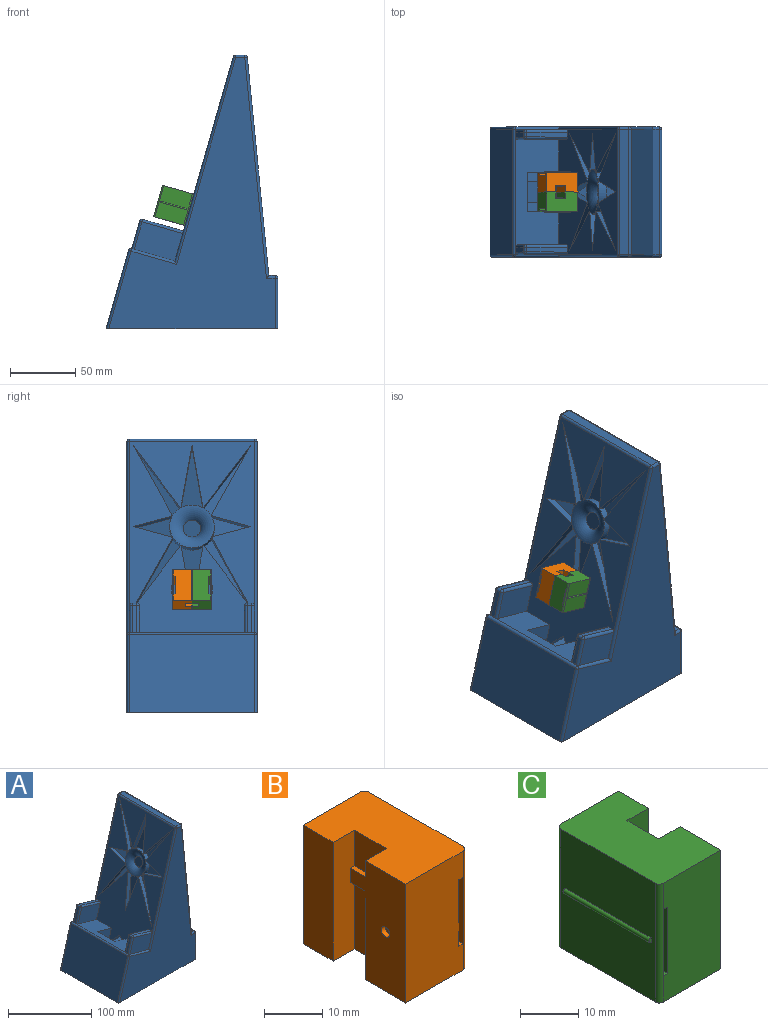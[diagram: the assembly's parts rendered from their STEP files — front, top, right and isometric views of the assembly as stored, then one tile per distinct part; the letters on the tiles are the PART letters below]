
ASSEMBLY  parts=3 mates=2
PART A: 139 faces, bbox 131.9x100x210.6 mm
  f0: plane 201.07x93mm, normal (0.96,0,-0.27), area 16114.9mm2, adj f1,f2,f3,f22,f23,f24,f25,f26
  f1: plane 6.2x1.71mm, normal (0.02,0,-1), area 5.3mm2, adj f0,f3,f137
  f2: plane 6.2x1.71mm, normal (0.02,0,-1), area 5.3mm2, adj f0,f98,f138
  f3: plane 24.74x13.23mm, normal (0,-1,0), area 152mm2, adj f0,f1,f11,f100
  f4: plane 5x1.82mm, normal (0.42,-0.91,0), area 5mm2, adj f9,f127,f134,f135,f136
  f5: plane 5x1.98mm, normal (0.99,-0.13,0), area 5mm2, adj f9,f125,f131,f132,f133
  f6: plane 5x1.98mm, normal (-0.99,0.13,0), area 5mm2, adj f9,f125,f131,f132,f133
  f7: plane 5x1.43mm, normal (-0.71,-0.7,0), area 5mm2, adj f9,f124,f128,f129,f130
  f8: plane 5x1.43mm, normal (0.71,0.7,0), area 5mm2, adj f9,f124,f128,f129,f130
  f9: plane 121.48x32.21mm, normal (0,0,1), area 3070.3mm2, adj f4,f5,f6,f7,f8,f16,f17,f24
  f10: plane 96x33.08mm, normal (0.27,0,0.96), area 2022.9mm2, adj f11,f20,f21,f57,f84,f88,f89,f104
  f11: plane 200.88x96mm, normal (-0.96,0,0.27), area 12526.6mm2, adj f3,f10,f20,f21,f24,f25,f27,f28
  f12: plane 131.88x100mm, normal (0,0,-1), area 13184.7mm2, adj f13,f51,f53,f85,f91,f92,f93,f97
  f13: plane 208x127.8mm, normal (0,-1,0), area 12025.5mm2, adj f12,f18,f73,f77,f82,f84,f85,f93
  f14: plane 96x5mm, normal (0,0,1), area 479.5mm2, adj f18,f19,f52,f95
  f15: plane 16x9.77mm, normal (0,0,-1), area 156.4mm2, adj f16,f17,f54,f92
  f16: plane 13.88x8.4mm, normal (0,1,0), area 80.6mm2, adj f9,f15,f23,f54,f65,f92
  f17: plane 13.88x8.4mm, normal (0,-1,0), area 80.6mm2, adj f9,f15,f22,f54,f61,f92
  f18: cylinder r=2mm len=6.81mm, axis (-1,0,0), area 17.8mm2, adj f13,f14,f73,f94
  f19: cylinder r=2mm len=6.81mm, axis (1,0,0), area 17.8mm2, adj f14,f51,f75,f96
  f20: plane 51.2x36.71mm, normal (0,-1,0), area 1128.6mm2, adj f10,f11,f57,f58,f70,f71,f72
  f21: plane 51.2x36.71mm, normal (0,1,0), area 1128.6mm2, adj f10,f11,f57,f58,f67,f68,f69
  f22: plane 77.33x40mm, normal (0,0,1), area 2508.9mm2, adj f0,f17,f25,f54,f56,f61,f62,f63
  f23: plane 77.33x37mm, normal (0,0,1), area 2312.4mm2, adj f0,f16,f24,f54,f55,f64,f65,f66
  f24: plane 37.7x8.4mm, normal (0,1,0), area 234.5mm2, adj f0,f9,f11,f23,f58,f59,f60,f64
  f25: plane 37.7x8.4mm, normal (0,-1,0), area 234.5mm2, adj f0,f9,f11,f22,f58,f59,f60,f62
  f26: cylinder r=17.15mm len=7.66mm, axis (-0.96,0,0.27), area 52.7mm2, adj f0,f27,f28,f101
  f27: plane 49.59x36.3mm, normal (-0.16,0.81,-0.57), area 365.4mm2, adj f0,f11,f26,f28,f101
  f28: plane 55.63x30.11mm, normal (0.13,-0.88,0.45), area 377.4mm2, adj f0,f11,f26,f27,f101
  f29: cylinder r=17.15mm len=17.03mm, axis (-0.96,0,0.27), area 105.4mm2, adj f0,f30,f31,f101
  f30: plane 49.43x19.37mm, normal (0.05,-0.99,0.16), area 298.6mm2, adj f0,f11,f29,f31,f101
  f31: plane 49.56x19.41mm, normal (0.05,0.99,0.16), area 299.6mm2, adj f0,f11,f29,f30,f101
  f32: cylinder r=17.15mm len=7.57mm, axis (-0.96,0,0.27), area 52.7mm2, adj f0,f33,f34,f101
  f33: plane 55.41x30.24mm, normal (-0.13,-0.88,-0.46), area 376.5mm2, adj f0,f11,f32,f34,f101
  f34: plane 49.46x36.53mm, normal (0.16,0.81,0.57), area 365.5mm2, adj f0,f11,f32,f33,f101
  f35: cylinder r=17.15mm len=17.98mm, axis (-0.96,0,0.27), area 105.2mm2, adj f0,f36,f37,f101
  f36: plane 30.05x9.7mm, normal (-0.26,-0.27,-0.93), area 184.7mm2, adj f0,f11,f35,f37,f101
  f37: plane 30.18x9.92mm, normal (0.26,-0.27,0.92), area 185.8mm2, adj f0,f11,f35,f36,f101
  f38: cylinder r=17.15mm len=17.03mm, axis (-0.96,0,0.27), area 105.4mm2, adj f0,f39,f40,f101
  f39: plane 49.44x19.36mm, normal (-0.05,0.99,-0.16), area 298.6mm2, adj f0,f11,f38,f40,f101
  f40: plane 49.56x19.4mm, normal (-0.05,-0.99,-0.16), area 299.6mm2, adj f0,f11,f38,f39,f101
  f41: cylinder r=17.15mm len=7.57mm, axis (-0.96,0,0.27), area 52.7mm2, adj f0,f42,f43,f101
  f42: plane 55.42x30.24mm, normal (0.13,0.88,0.46), area 376.5mm2, adj f0,f11,f41,f43,f101
  f43: plane 49.47x36.53mm, normal (-0.16,-0.81,-0.57), area 365.5mm2, adj f0,f11,f41,f42,f101
  f44: cylinder r=17.15mm len=7.66mm, axis (-0.96,0,0.27), area 52.7mm2, adj f0,f45,f46,f101
  f45: plane 49.59x36.3mm, normal (0.16,-0.81,0.57), area 365.4mm2, adj f0,f11,f44,f46,f101
  f46: plane 55.63x30.11mm, normal (-0.13,0.88,-0.45), area 377.4mm2, adj f0,f11,f44,f45,f101
  f47: cylinder r=17.15mm len=17.98mm, axis (-0.96,0,0.27), area 105.2mm2, adj f0,f48,f49,f101
  f48: plane 30.05x9.62mm, normal (0.27,0.27,0.93), area 184.5mm2, adj f0,f11,f47,f49,f101
  f49: plane 30.18x10mm, normal (-0.26,0.28,-0.92), area 185.9mm2, adj f0,f11,f47,f48,f101
  f50: plane 96x6.98mm, normal (0,0,1), area 669.7mm2, adj f76,f77,f80,f81
  f51: plane 208x127.8mm, normal (0,1,0), area 12025.5mm2, adj f12,f19,f75,f80,f86,f88,f91,f97
  f52: plane 167.24x96mm, normal (1,0,0.1), area 16132.7mm2, adj f14,f73,f75,f76
  f53: plane 96x60.08mm, normal (-0.96,0,0.27), area 5998.6mm2, adj f12,f85,f89,f91
  f54: plane 201.07x93mm, normal (-1,0,-0.1), area 18661.8mm2, adj f0,f15,f16,f17,f22,f23,f55,f56
  f55: plane 201.07x77.33mm, normal (0,1,0), area 7774.9mm2, adj f0,f23,f54
  f56: plane 201.07x77.33mm, normal (0,-1,0), area 7774.9mm2, adj f0,f22,f54
  f57: plane 44.32x30mm, normal (0.96,0,-0.27), area 1383mm2, adj f10,f20,f21,f58
  f58: plane 30x24.04mm, normal (0.27,0,0.96), area 416.4mm2, adj f11,f20,f21,f24,f25,f57,f59
  f59: plane 16x9.61mm, normal (0,0,-1), area 153.8mm2, adj f24,f25,f58,f60
  f60: plane 16x8.4mm, normal (1,0,0), area 134.4mm2, adj f9,f24,f25,f59
  f61: plane 8.36x0.39mm, normal (-1,0,0), area 3.3mm2, adj f9,f17,f22,f63
  f62: plane 8.36x0.39mm, normal (1,0,0), area 3.3mm2, adj f9,f22,f25,f63
  f63: plane 69.9x0.39mm, normal (0,-1,0), area 27.4mm2, adj f9,f22,f61,f62
  f64: plane 7.85x0.39mm, normal (1,0,0), area 3.1mm2, adj f9,f23,f24,f66
  f65: plane 7.85x0.39mm, normal (-1,0,0), area 3.1mm2, adj f9,f16,f23,f66
  f66: plane 69.9x0.39mm, normal (0,1,0), area 27.4mm2, adj f9,f23,f64,f65
  f67: cylinder r=0.5mm len=23.25mm, axis (-0.96,0,0.27), area 37.5mm2, adj f21,f68,f69
  f68: plane 0.96x0.5mm, normal (-0.96,0,0.27), area 0.4mm2, adj f21,f67
  f69: plane 0.96x0.5mm, normal (0.96,0,-0.27), area 0.4mm2, adj f21,f67
  f70: cylinder r=0.5mm len=23.25mm, axis (-0.96,0,0.27), area 37.5mm2, adj f20,f71,f72
  f71: plane 0.96x0.5mm, normal (-0.96,0,0.27), area 0.4mm2, adj f20,f70
  f72: plane 0.96x0.5mm, normal (0.96,0,-0.27), area 0.4mm2, adj f20,f70
  f73: cylinder r=2mm len=169.24mm, axis (-0.1,0,1), area 530mm2, adj f13,f18,f52,f74
  f74: sphere r=2mm, area 5.9mm2, adj f73,f76,f77
  f75: cylinder r=2mm len=169.24mm, axis (0.1,0,-1), area 530mm2, adj f19,f51,f52,f78
  f76: cylinder r=2mm len=96mm, axis (0,-1,0), area 282.7mm2, adj f50,f52,f74,f78
  f77: cylinder r=2mm len=6.98mm, axis (1,0,0), area 21.9mm2, adj f13,f50,f74,f79
  f78: sphere r=2mm, area 5.9mm2, adj f75,f76,f80
  f79: sphere r=2mm, area 5.2mm2, adj f77,f81,f82
  f80: cylinder r=2mm len=6.98mm, axis (-1,0,0), area 21.9mm2, adj f50,f51,f78,f83
  f81: cylinder r=2mm len=96mm, axis (0,-1,0), area 248.1mm2, adj f11,f50,f79,f83
  f82: cylinder r=2mm len=159.03mm, axis (-0.27,0,-0.96), area 513.8mm2, adj f11,f13,f79,f84,f106
  f83: sphere r=2mm, area 5.2mm2, adj f80,f81,f86
  f84: cylinder r=2mm len=35.55mm, axis (-0.96,0,0.27), area 110.4mm2, adj f10,f13,f82,f87,f106
  f85: cylinder r=2mm len=60.63mm, axis (-0.27,0,-0.96), area 195.7mm2, adj f12,f13,f53,f87
  f86: cylinder r=2mm len=159.03mm, axis (0.27,0,0.96), area 513.8mm2, adj f11,f51,f83,f88,f103
  f87: sphere r=2mm, area 6.3mm2, adj f84,f85,f89
  f88: cylinder r=2mm len=35.55mm, axis (0.96,0,-0.27), area 110.4mm2, adj f10,f51,f86,f90,f103
  f89: cylinder r=2mm len=96mm, axis (0,-1,0), area 301.6mm2, adj f10,f53,f87,f90
  f90: sphere r=2mm, area 6.3mm2, adj f88,f89,f91
  f91: cylinder r=2mm len=60.63mm, axis (0.27,0,0.96), area 195.7mm2, adj f12,f51,f53,f90
  f92: plane 96x38.96mm, normal (1,0,0), area 3605.6mm2, adj f9,f12,f15,f16,f17,f93,f95,f97
  f93: cylinder r=2mm len=38.96mm, axis (0,0,1), area 122.4mm2, adj f12,f13,f92,f94
  f94: sphere r=2mm, area 6.3mm2, adj f18,f93,f95
  f95: cylinder r=2mm len=96mm, axis (0,1,0), area 301.6mm2, adj f14,f92,f94,f96
  f96: sphere r=2mm, area 6.3mm2, adj f19,f95,f97
  f97: cylinder r=2mm len=38.96mm, axis (0,0,1), area 122.4mm2, adj f12,f51,f92,f96
  f98: plane 24.74x13.23mm, normal (0,1,0), area 152mm2, adj f0,f2,f11,f99
  f99: plane 6.16x4.71mm, normal (0,0,1), area 29mm2, adj f0,f11,f24,f98
  f100: plane 6.16x4.23mm, normal (0,0,1), area 26mm2, adj f0,f3,f11,f25
  f101: torus R=17.68mm, axis (0.96,0,-0.27), area 898.6mm2, adj f0,f11,f26,f27,f28,f29,f30,f31
  f102: plane 31.15x8.91mm, normal (0.27,0,0.96), area 121.5mm2, adj f11,f118,f121,f123
  f103: plane 37.2x30.06mm, normal (0,1,0), area 712.8mm2, adj f86,f88,f117,f118
  f104: plane 37.2x30.06mm, normal (0,-1,0), area 712.8mm2, adj f10,f11,f120,f123
  f105: plane 21.15x6.05mm, normal (-0.96,0,0.27), area 82.5mm2, adj f10,f117,f120,f121
  f106: plane 37.2x30.06mm, normal (0,-1,0), area 712.8mm2, adj f82,f84,f113,f116
  f107: plane 31.15x8.91mm, normal (0.27,0,0.96), area 121.5mm2, adj f11,f111,f114,f116
  f108: plane 37.2x30.06mm, normal (0,1,0), area 712.8mm2, adj f10,f11,f110,f111
  f109: plane 21.15x6.05mm, normal (-0.96,0,0.27), area 82.5mm2, adj f10,f110,f113,f114
  f110: cylinder r=2mm len=21.7mm, axis (0.27,0,0.96), area 69.1mm2, adj f10,f108,f109,f112
  f111: cylinder r=2mm len=31.7mm, axis (0.96,0,-0.27), area 101.8mm2, adj f11,f107,f108,f112
  f112: sphere r=2mm, area 6.3mm2, adj f110,f111,f114
  f113: cylinder r=2mm len=21.7mm, axis (-0.27,0,-0.96), area 69.1mm2, adj f10,f106,f109,f115
  f114: cylinder r=2mm len=3.75mm, axis (0,-1,0), area 11.8mm2, adj f107,f109,f112,f115
  f115: sphere r=2mm, area 6.3mm2, adj f113,f114,f116
  f116: cylinder r=2mm len=31.7mm, axis (0.96,0,-0.27), area 101.8mm2, adj f11,f106,f107,f115
  f117: cylinder r=2mm len=21.7mm, axis (0.27,0,0.96), area 69.1mm2, adj f10,f103,f105,f119
  f118: cylinder r=2mm len=31.7mm, axis (-0.96,0,0.27), area 101.8mm2, adj f11,f102,f103,f119
  f119: sphere r=2mm, area 6.3mm2, adj f117,f118,f121
  f120: cylinder r=2mm len=21.7mm, axis (-0.27,0,-0.96), area 69.1mm2, adj f10,f104,f105,f122
  f121: cylinder r=2mm len=3.75mm, axis (0,-1,0), area 11.8mm2, adj f102,f105,f119,f122
  f122: sphere r=2mm, area 6.3mm2, adj f120,f121,f123
  f123: cylinder r=2mm len=31.7mm, axis (0.96,0,-0.27), area 101.8mm2, adj f11,f102,f104,f122
  f124: plane 5x1.62mm, normal (0.7,-0.71,0), area 11.3mm2, adj f7,f8,f9,f128
  f125: plane 5x2.24mm, normal (0.13,0.99,0), area 11.3mm2, adj f5,f6,f9,f133
  f126: plane 5x1.82mm, normal (-0.42,0.91,0), area 5mm2, adj f9,f127,f134,f135,f136
  f127: plane 5x2.05mm, normal (-0.91,-0.42,0), area 11.3mm2, adj f4,f9,f126,f136
  f128: plane 3.02x3.01mm, normal (-0.49,0.51,0.71), area 6.4mm2, adj f7,f8,f124,f129
  f129: plane 2.32x2.3mm, normal (0,0,-1), area 2.3mm2, adj f7,f8,f128,f130
  f130: plane 3x1.62mm, normal (-0.7,0.71,0), area 6.8mm2, adj f7,f8,f9,f129
  f131: plane 2.38x1.3mm, normal (0,0,-1), area 2.3mm2, adj f5,f6,f132,f133
  f132: plane 3x2.24mm, normal (-0.13,-0.99,0), area 6.8mm2, adj f5,f6,f9,f131
  f133: plane 2.51x2.29mm, normal (-0.1,-0.7,0.71), area 6.4mm2, adj f5,f6,f125,f131
  f134: plane 2.47x1.86mm, normal (0,0,-1), area 2.3mm2, adj f4,f126,f135,f136
  f135: plane 3x2.05mm, normal (0.91,0.42,0), area 6.8mm2, adj f4,f9,f126,f134
  f136: plane 2.89x2.76mm, normal (0.64,0.3,0.71), area 6.4mm2, adj f4,f126,f127,f134
  f137: plane 12.78x12.47mm, normal (-0.19,-0.73,-0.66), area 100.5mm2, adj f0,f1,f11,f138
  f138: plane 12.78x12.47mm, normal (-0.19,0.73,-0.66), area 100.5mm2, adj f0,f2,f11,f137
PART B: 25 faces, bbox 15.5x24.9x25 mm
  f0: plane 25x22.9mm, normal (1,0,0), area 551.6mm2, adj f6,f7,f20,f21,f22,f23,f24
  f1: plane 25x13.95mm, normal (0,1,0), area 334.7mm2, adj f6,f7,f8,f16,f18,f19,f24
  f2: plane 25x13.95mm, normal (0,-1,0), area 334.7mm2, adj f5,f6,f7,f16,f18,f19,f23
  f3: plane 7.75x7.5mm, normal (-1,0,0), area 58.1mm2, adj f4,f6,f9,f13
  f4: plane 25x5.17mm, normal (0,1,0), area 126.1mm2, adj f3,f5,f6,f7,f10,f13,f14,f15
  f5: plane 25x9.89mm, normal (-1,0,0), area 243.8mm2, adj f2,f4,f6,f7,f11
  f6: plane 24.9x14.95mm, normal (0,0,1), area 331.8mm2, adj f0,f1,f2,f3,f4,f5,f8,f9
  f7: plane 24.9x14.95mm, normal (0,0,-1), area 331.8mm2, adj f0,f1,f2,f4,f5,f8,f9,f10
  f8: plane 25x7.27mm, normal (-1,0,0), area 181.6mm2, adj f1,f6,f7,f9
  f9: plane 25x5.17mm, normal (0,-1,0), area 126.1mm2, adj f3,f6,f7,f8,f10,f13,f14,f15
  f10: plane 14.5x7.75mm, normal (-1,0,0), area 112.4mm2, adj f4,f7,f9,f14
  f11: cylinder r=1.03mm len=2.05mm, axis (-1,0,0), area 6.4mm2, adj f5,f12
  f12: plane 2.05x2.05mm, normal (-1,0,0), area 3.3mm2, adj f11
  f13: plane 7.75x1mm, normal (0,0,1), area 7.7mm2, adj f3,f4,f9,f15
  f14: plane 7.75x1mm, normal (0,0,-1), area 7.7mm2, adj f4,f9,f10,f15
  f15: plane 7.75x3mm, normal (-1,0,0), area 23.3mm2, adj f4,f9,f13,f14
  f16: plane 24.9x1mm, normal (0,0,-1), area 24.9mm2, adj f1,f2,f17,f19
  f17: plane 24.9x14mm, normal (-1,0,0), area 348.6mm2, adj f16,f18,f23,f24
  f18: plane 24.9x1mm, normal (0,0,1), area 24.9mm2, adj f1,f2,f17,f19
  f19: plane 24.9x14mm, normal (1,0,0), area 348.6mm2, adj f1,f2,f16,f18
  f20: plane 1x0.5mm, normal (0,-1,0), area 0.4mm2, adj f0,f21
  f21: cylinder r=0.5mm len=20.9mm, axis (0,1,0), area 32.8mm2, adj f0,f20,f22
  f22: plane 1x0.5mm, normal (0,1,0), area 0.4mm2, adj f0,f21
  f23: cylinder r=1mm len=25mm, axis (0,0,1), area 39.3mm2, adj f0,f2,f6,f7,f17
  f24: cylinder r=1mm len=25mm, axis (0,0,-1), area 39.3mm2, adj f0,f1,f6,f7,f17
PART C: 26 faces, bbox 16.5x24.9x25 mm
  f0: plane 25x13.95mm, normal (0,1,0), area 334.8mm2, adj f5,f6,f7,f18,f19,f20,f24
  f1: plane 25x13.95mm, normal (0,-1,0), area 334.8mm2, adj f4,f5,f6,f18,f19,f20,f25
  f2: plane 14.5x7.75mm, normal (1,0,0), area 112.4mm2, adj f3,f6,f9,f15
  f3: plane 25x5.17mm, normal (0,1,0), area 126.1mm2, adj f2,f4,f5,f6,f10,f14,f15,f16
  f4: plane 25x9.89mm, normal (1,0,0), area 244mm2, adj f1,f3,f5,f6,f11
  f5: plane 24.9x14.95mm, normal (0,0,1), area 331.8mm2, adj f0,f1,f3,f4,f7,f8,f9,f10
  f6: plane 24.9x14.95mm, normal (0,0,-1), area 331.8mm2, adj f0,f1,f2,f3,f4,f7,f8,f9
  f7: plane 25x7.27mm, normal (1,0,0), area 181.6mm2, adj f0,f5,f6,f9
  f8: plane 25x22.9mm, normal (-1,0,0), area 551.6mm2, adj f5,f6,f21,f22,f23,f24,f25
  f9: plane 25x5.17mm, normal (0,-1,0), area 126.1mm2, adj f2,f5,f6,f7,f10,f14,f15,f16
  f10: plane 7.75x7.5mm, normal (1,0,0), area 58.1mm2, adj f3,f5,f9,f14
  f11: cylinder r=1mm len=2mm, axis (-1,0,0), area 0.6mm2, adj f4,f13
  f12: plane 0.2x0.2mm, normal (1,0,0), area 0mm2, adj f13
  f13: torus R=0.1mm, axis (1,0,0), area 6mm2, adj f11,f12
  f14: plane 7.75x1mm, normal (0,0,1), area 7.8mm2, adj f3,f9,f10,f16
  f15: plane 7.75x1mm, normal (0,0,-1), area 7.8mm2, adj f2,f3,f9,f16
  f16: plane 7.75x3mm, normal (1,0,0), area 23.3mm2, adj f3,f9,f14,f15
  f17: plane 24.9x14mm, normal (1,0,0), area 348.6mm2, adj f18,f20,f24,f25
  f18: plane 24.9x1mm, normal (0,0,-1), area 24.9mm2, adj f0,f1,f17,f19
  f19: plane 24.9x14mm, normal (-1,0,0), area 348.6mm2, adj f0,f1,f18,f20
  f20: plane 24.9x1mm, normal (0,0,1), area 24.9mm2, adj f0,f1,f17,f19
  f21: plane 1x0.5mm, normal (0,-1,0), area 0.4mm2, adj f8,f23
  f22: plane 1x0.5mm, normal (0,1,0), area 0.4mm2, adj f8,f23
  f23: cylinder r=0.5mm len=20.9mm, axis (0,1,0), area 32.8mm2, adj f8,f21,f22
  f24: cylinder r=1mm len=25mm, axis (0,0,-1), area 39.3mm2, adj f0,f5,f6,f8,f17
  f25: cylinder r=1mm len=25mm, axis (0,0,1), area 39.3mm2, adj f1,f5,f6,f8,f17
PLACE A t=(-56.57,29.34,9.38)mm fixed
PLACE B rot(axis=(0.14,0.14,0.98),91.1deg) t=(-88.34,72.63,-10.75)mm
PLACE C rot(axis=(0.14,0.14,0.98),91.1deg) t=(-84.87,2.66,-11.74)mm
MATE slider B.f6 <-> A.f10  axis (0.27,0,0.96) through (-85.71,-20.66,14.51)mm
MATE fastened C.f13 <-> B.f11  axis (0,1,0) through (-69.96,-20.66,-3)mm
